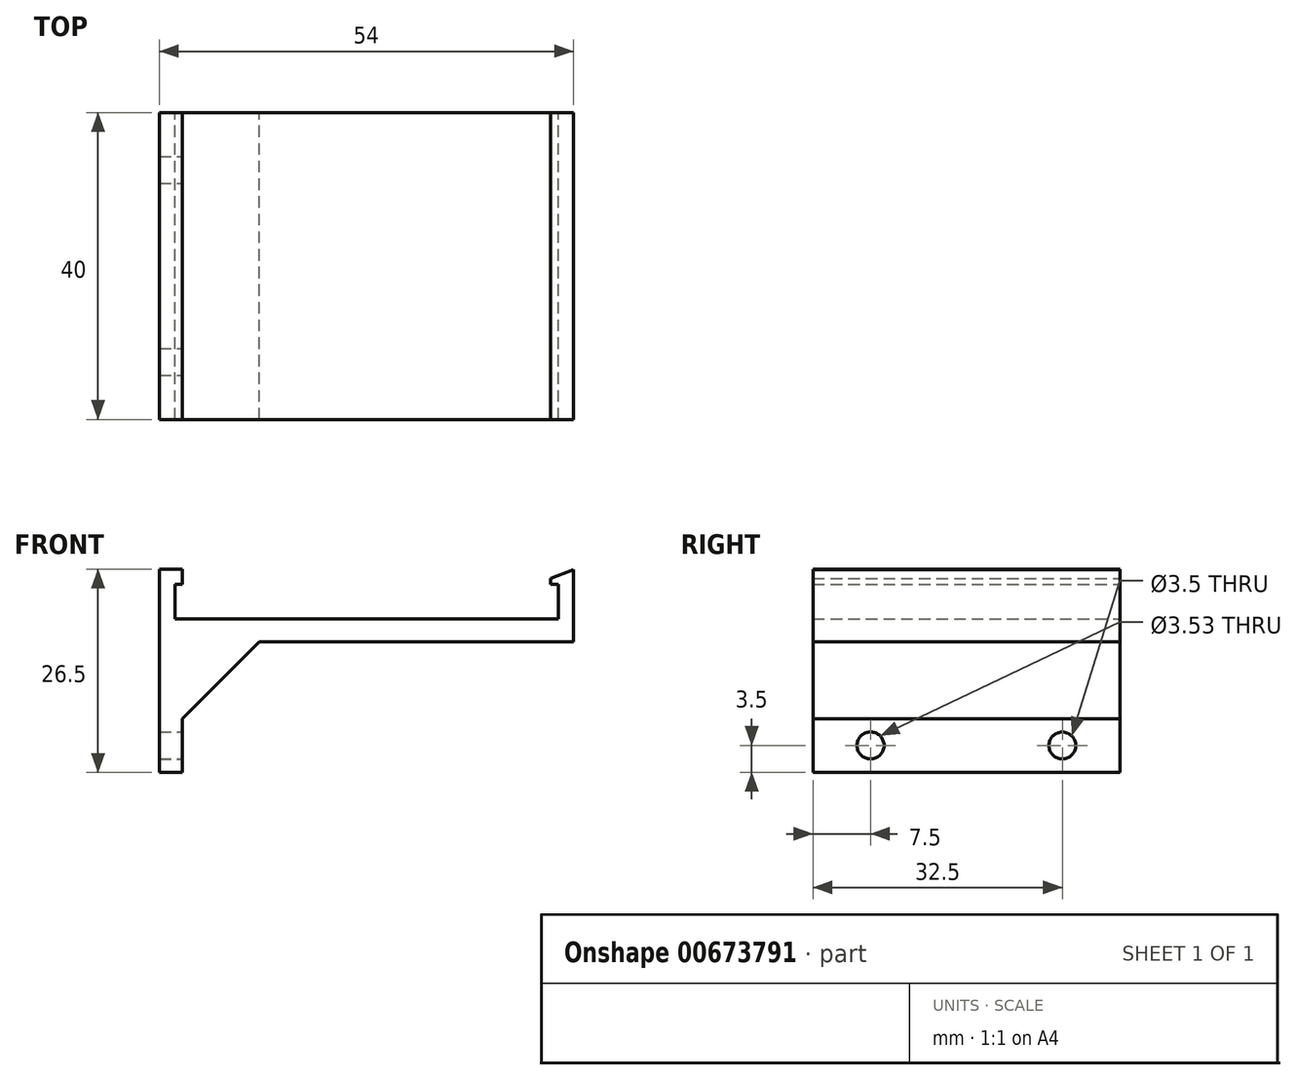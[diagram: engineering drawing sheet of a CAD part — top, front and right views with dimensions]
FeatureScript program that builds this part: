
annotation { "Feature Type Name" : "Feature", "Feature Type Description" : "" }
export const myFeature = defineFeature(function(context is Context, id is Id, definition is map)
    precondition{}
    {
        {
            var Q0;
            Q0=qCreatedBy(makeId("Front.planeOp"),FACE);
            var sketch = newSketch(context, id + "F0", { "sketchPlane" : qUnion([Q0])});
            skLineSegment(sketch, "E0", {"start": v(0, 0) * mm, "end": v(0, -20) * mm});
            skLineSegment(sketch, "E1", {"start": v(0, -20) * mm, "end": v(3, -20) * mm});
            skLineSegment(sketch, "E2", {"start": v(3, -20) * mm, "end": v(3, -3) * mm});
            skLineSegment(sketch, "E3", {"start": v(3, -3) * mm, "end": v(54, -3) * mm});
            skLineSegment(sketch, "E4", {"start": v(54, -3) * mm, "end": v(54, 0) * mm});
            skLineSegment(sketch, "E5", {"start": v(52, 0) * mm, "end": v(2, 0) * mm});
            skLineSegment(sketch, "E6", {"start": v(54, 0) * mm, "end": v(54, 6.4) * mm});
            skLineSegment(sketch, "E7", {"start": v(51, 4.5) * mm, "end": v(52, 4.5) * mm});
            skLineSegment(sketch, "E8", {"start": v(52, 4.5) * mm, "end": v(52, 0) * mm});
            skLineSegment(sketch, "E9", {"start": v(0, 0) * mm, "end": v(0, 6.5) * mm});
            skLineSegment(sketch, "E10", {"start": v(0, 6.5) * mm, "end": v(3, 6.5) * mm});
            skLineSegment(sketch, "E11", {"start": v(3, 6.5) * mm, "end": v(3, 4.5) * mm});
            skLineSegment(sketch, "E12", {"start": v(3, 4.5) * mm, "end": v(2, 4.5) * mm});
            skLineSegment(sketch, "E13", {"start": v(2, 4.5) * mm, "end": v(2, 0) * mm});
            skLineSegment(sketch, "E14", {"start": v(51, 4.5) * mm, "end": v(51, 5.27) * mm});
            skLineSegment(sketch, "E15", {"start": v(51, 5.27) * mm, "end": v(54, 6.4) * mm});
            skSolve(sketch);
        }
        {
            var Q0;
            Q0 = qSketchRegion(id + "F0", true);
            extrude(context, id + "F1", {"entities" : qUnion([Q0]), "depth" : 40 * mm, "offsetDistance" : 25 * mm});
        }
        {
            var Q0;
            Q0=makeQuery(id+"F1.opExtrude","SWEPT_EDGE",EDGE,{"disambiguationData":[OSD([sQuery(id+"F0.wireOp",EDGE,"E2"),sQuery(id+"F0.wireOp",EDGE,"E3")])]});
            chamfer(context, id + "F2", {"entities" : qUnion([Q0]), "width" : 10 * mm, "tangentPropagation" : true});
        }
        {
            var Q0;
            Q0=makeQuery(id+"F1.opExtrude","SWEPT_FACE",FACE,{"disambiguationData":[OSD([sQuery(id+"F0.wireOp",EDGE,"E2")])]});
            var sketch = newSketch(context, id + "F3", { "sketchPlane" : qUnion([Q0])});
            skCircle(sketch, "E16", {"center": v(-32.5, -16.5) * mm, "radius": 1.76 * mm});
            skCircle(sketch, "E17", {"center": v(-7.5, -16.5) * mm, "radius": 1.75 * mm});
            skSolve(sketch);
        }
        {
            var Q0;
            Q0 = qSketchRegion(id + "F3", true);
            extrude(context, id + "F4", {"entities" : qUnion([Q0]), "operationType" : NewBodyOperationType.REMOVE, "oppositeDirection" : true, "depth" : 25 * mm, "offsetDistance" : 25 * mm});
        }
    });
